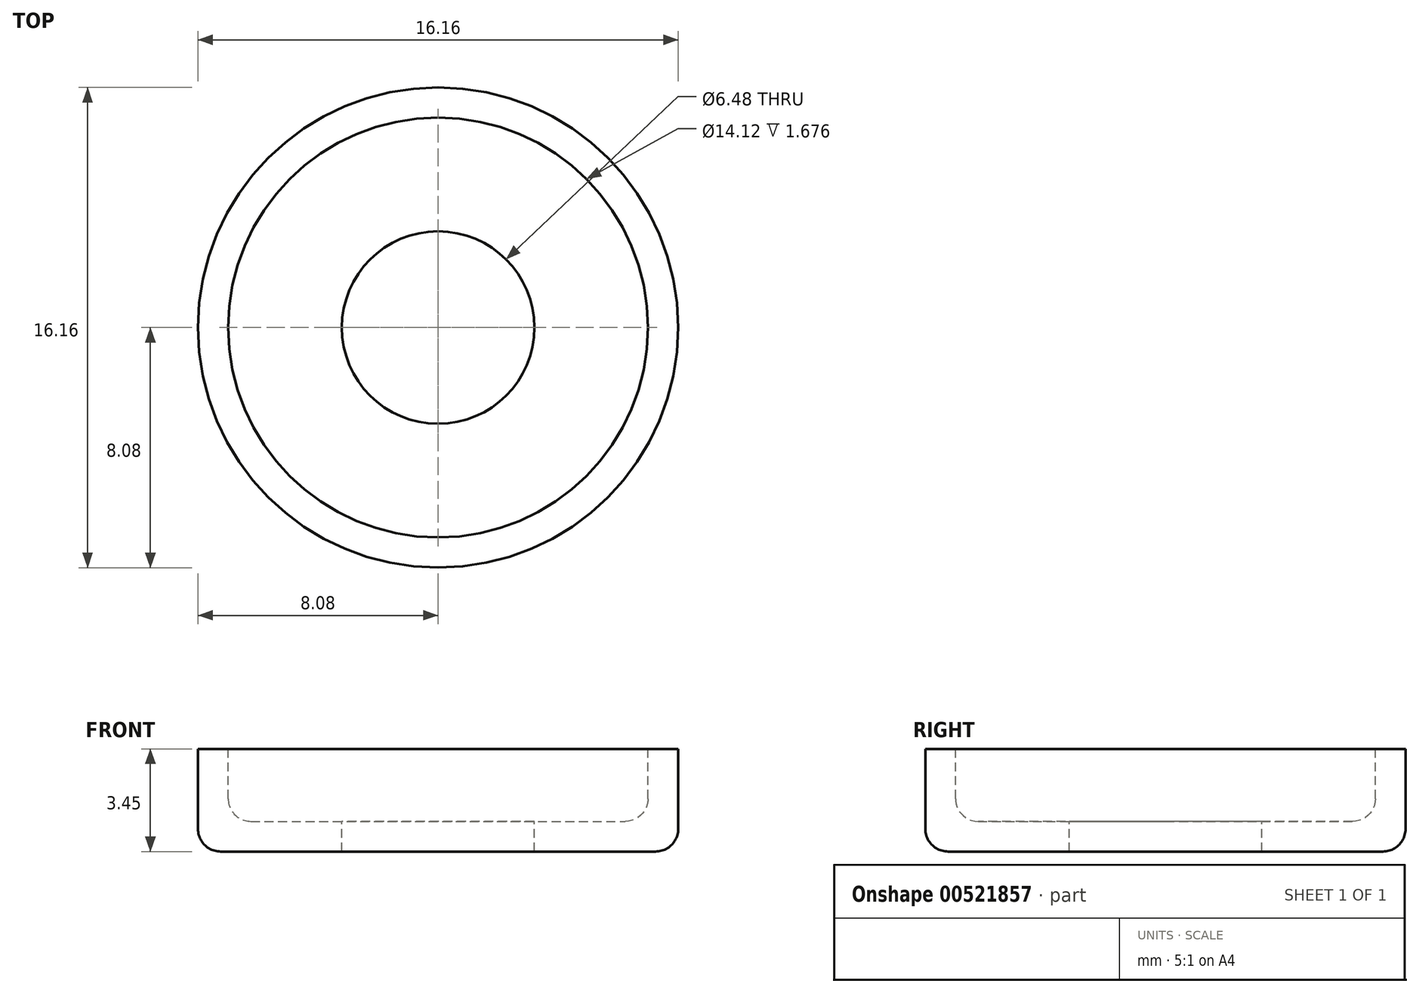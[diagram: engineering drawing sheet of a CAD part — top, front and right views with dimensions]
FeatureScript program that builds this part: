
annotation { "Feature Type Name" : "Feature", "Feature Type Description" : "" }
export const myFeature = defineFeature(function(context is Context, id is Id, definition is map)
    precondition{}
    {
        {
            var Q0;
            Q0=qCreatedBy(makeId("Front.planeOp"),FACE);
            var sketch = newSketch(context, id + "F0", { "sketchPlane" : qUnion([Q0])});
            skLineSegment(sketch, "E0", {"start": v(-8.08, 3.45) * mm, "end": v(-8.08, 0) * mm});
            skLineSegment(sketch, "E1", {"start": v(-8.08, 0) * mm, "end": v(-3.24, 0) * mm});
            skLineSegment(sketch, "E2", {"start": v(0, 0) * mm, "end": v(0, -2.63) * mm, "construction": true});
            skLineSegment(sketch, "E3", {"start": v(-8.08, 3.45) * mm, "end": v(-7.06, 3.45) * mm});
            skLineSegment(sketch, "E4", {"start": v(-7.06, 3.45) * mm, "end": v(-7.06, 1.02) * mm});
            skLineSegment(sketch, "E5", {"start": v(-7.06, 1.02) * mm, "end": v(-3.24, 1.02) * mm});
            skLineSegment(sketch, "E6", {"start": v(-3.24, 1.02) * mm, "end": v(-3.24, 0) * mm});
            skSolve(sketch);
        }
        {
            var Q0;
            Q0 = qSketchRegion(id + "F0", true);
            var Q1;
            Q1=sQuery(id+"F0.wireOp",EDGE,"E2");
            revolve(context, id + "F1", {"entities" : qUnion([Q0]), "axis" : qUnion([Q1]), "revolveType" : RevolveType.FULL});
        }
        {
            var Q0;
            Q0=makeQuery(id+"F1.opRevolve","SWEPT_EDGE",EDGE,{"disambiguationData":[OSD([sQuery(id+"F0.wireOp",EDGE,"E4"),sQuery(id+"F0.wireOp",EDGE,"E5")])]});
            var Q1;
            Q1=makeQuery(id+"F1.opRevolve","SWEPT_EDGE",EDGE,{"disambiguationData":[OSD([sQuery(id+"F0.wireOp",EDGE,"E0"),sQuery(id+"F0.wireOp",EDGE,"E1")])]});
            fillet(context, id + "F2", {"entities" : qUnion([Q0, Q1]), "radius" : 0.76 * mm, "tangentPropagation" : true, "allowEdgeOverflow" : false});
        }
    });
